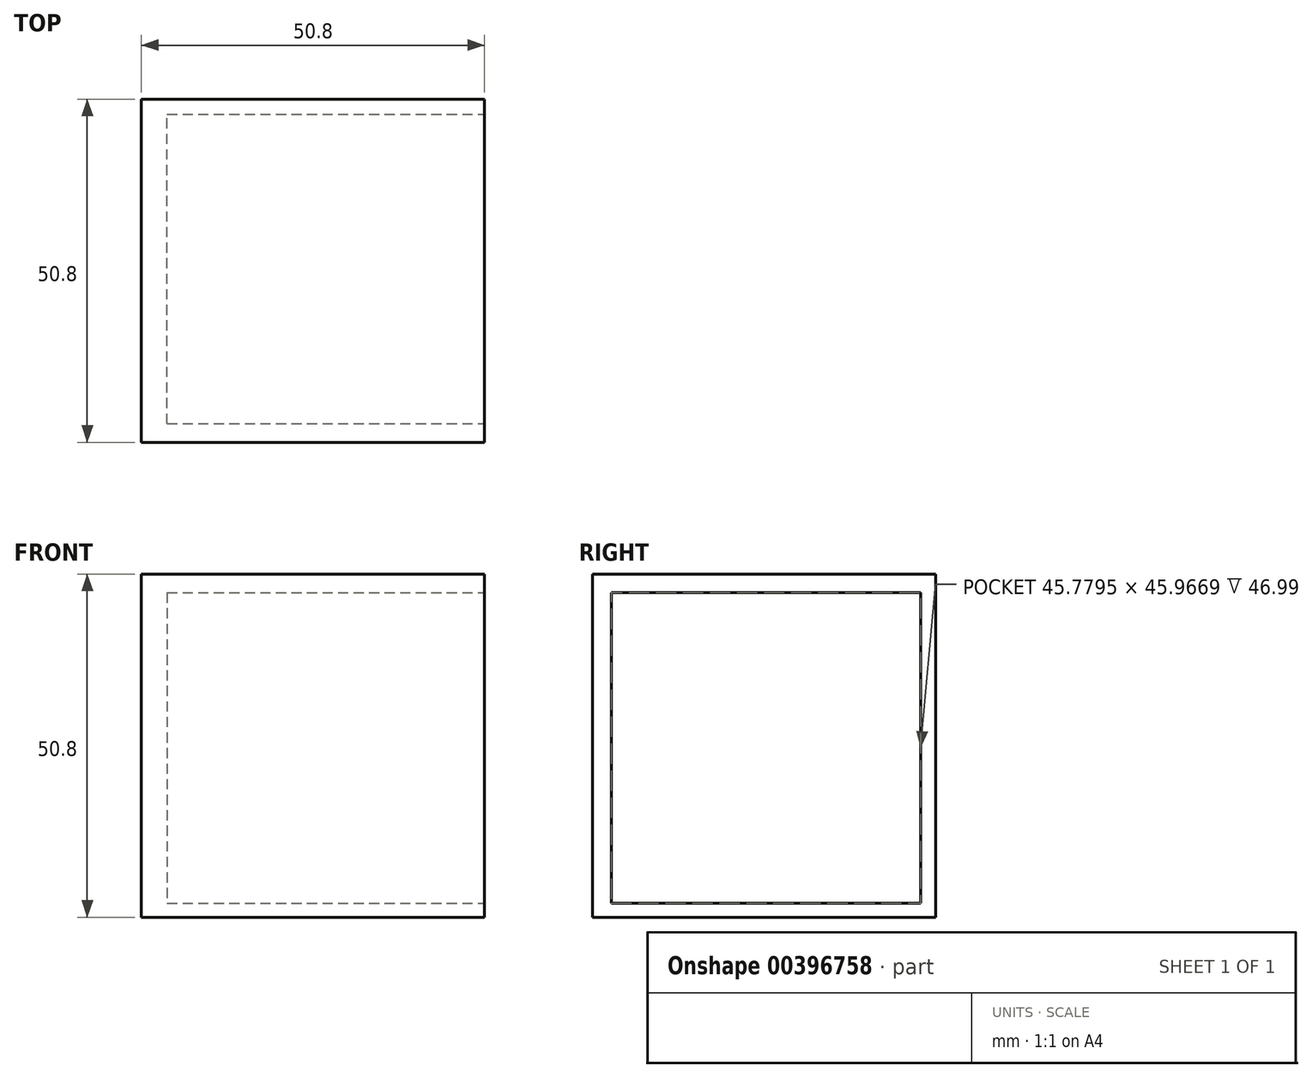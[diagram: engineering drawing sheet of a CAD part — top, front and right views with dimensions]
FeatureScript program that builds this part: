
annotation { "Feature Type Name" : "Feature", "Feature Type Description" : "" }
export const myFeature = defineFeature(function(context is Context, id is Id, definition is map)
    precondition{}
    {
        {
            var Q0;
            Q0=qCreatedBy(makeId("Front.planeOp"),FACE);
            var sketch = newSketch(context, id + "F0", { "sketchPlane" : qUnion([Q0])});
            skLineSegment(sketch, "E0.bottom", {"start": v(0, 0) * mm, "end": v(50.8, 0) * mm});
            skLineSegment(sketch, "E0.top", {"start": v(0, 50.8) * mm, "end": v(50.8, 50.8) * mm});
            skLineSegment(sketch, "E0.left", {"start": v(0, 0) * mm, "end": v(0, 50.8) * mm});
            skLineSegment(sketch, "E0.right", {"start": v(50.8, 0) * mm, "end": v(50.8, 50.8) * mm});
            skSolve(sketch);
        }
        {
            var Q0;
            Q0 = qSketchRegion(id + "F0", true);
            extrude(context, id + "F1", {"entities" : qUnion([Q0]), "depth" : 50.8 * mm});
        }
        {
            var Q0;
            Q0=makeQuery(id+"F1.opExtrude","SWEPT_FACE",FACE,{"disambiguationData":[OSD([sQuery(id+"F0.wireOp",EDGE,"E0.right")])]});
            var sketch = newSketch(context, id + "F2", { "sketchPlane" : qUnion([Q0])});
            skLineSegment(sketch, "E1.bottom", {"start": v(-50.8, 49.12) * mm, "end": v(-50.8, 49.12) * mm});
            skLineSegment(sketch, "E1.top", {"start": v(-50.8, 45.86) * mm, "end": v(-50.8, 45.86) * mm});
            skLineSegment(sketch, "E1.left", {"start": v(-50.8, 49.12) * mm, "end": v(-50.8, 45.86) * mm});
            skLineSegment(sketch, "E2.bottom", {"start": v(-48.04, 48.04) * mm, "end": v(-2.26, 48.04) * mm});
            skLineSegment(sketch, "E2.top", {"start": v(-48.04, 2.07) * mm, "end": v(-2.26, 2.07) * mm});
            skLineSegment(sketch, "E2.left", {"start": v(-48.04, 48.04) * mm, "end": v(-48.04, 2.07) * mm});
            skLineSegment(sketch, "E2.right", {"start": v(-2.26, 48.04) * mm, "end": v(-2.26, 2.07) * mm});
            skSolve(sketch);
        }
        {
            var Q0;
            Q0=makeQuery(id+"F2.imprint","IMPRINT",FACE,{"disambiguationData":[TD([[makeQuery(id+"F2.imprint","IMPRINT",EDGE,{"derivedFrom":sQuery(id+"F2.wireOp",EDGE,"E2.bottom")}),-1.0]])]});
            extrude(context, id + "F3", {"entities" : qUnion([Q0]), "operationType" : NewBodyOperationType.REMOVE, "oppositeDirection" : true, "depth" : 47 * mm});
        }
    });
